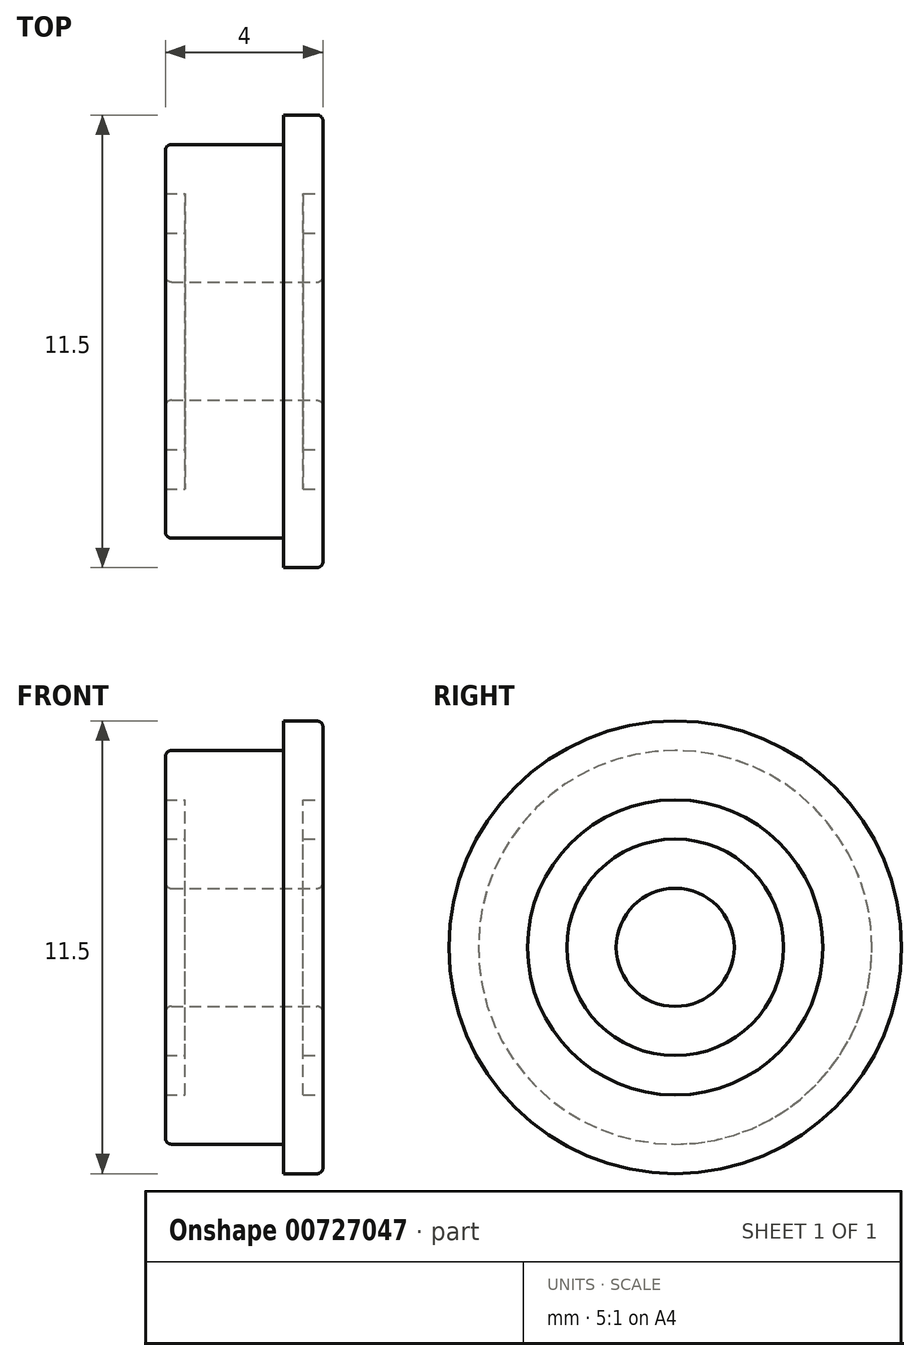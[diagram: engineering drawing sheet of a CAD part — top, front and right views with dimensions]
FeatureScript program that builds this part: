
annotation { "Feature Type Name" : "Feature", "Feature Type Description" : "" }
export const myFeature = defineFeature(function(context is Context, id is Id, definition is map)
    precondition{}
    {
        {
            var Q0;
            Q0=qCreatedBy(makeId("Front.planeOp"),FACE);
            var sketch = newSketch(context, id + "F0", { "sketchPlane" : qUnion([Q0])});
            skLineSegment(sketch, "E0", {"start": v(-2, 1.5) * mm, "end": v(2, 1.5) * mm});
            skLineSegment(sketch, "E1", {"start": v(2, 1.5) * mm, "end": v(2, 2.75) * mm});
            skLineSegment(sketch, "E2", {"start": v(2, 3.75) * mm, "end": v(2, 5.75) * mm});
            skLineSegment(sketch, "E3", {"start": v(2, 5.75) * mm, "end": v(1, 5.75) * mm});
            skLineSegment(sketch, "E4", {"start": v(1, 5.75) * mm, "end": v(1, 5) * mm});
            skLineSegment(sketch, "E5", {"start": v(1, 5) * mm, "end": v(-2, 5) * mm});
            skLineSegment(sketch, "E6", {"start": v(-2, 5) * mm, "end": v(-2, 3.75) * mm});
            skLineSegment(sketch, "E7", {"start": v(-2, 3.75) * mm, "end": v(-1.5, 3.75) * mm});
            skLineSegment(sketch, "E8", {"start": v(-1.5, 3.75) * mm, "end": v(-1.5, 2.75) * mm});
            skLineSegment(sketch, "E9", {"start": v(-1.5, 2.75) * mm, "end": v(-2, 2.75) * mm});
            skLineSegment(sketch, "E10", {"start": v(-2, 2.75) * mm, "end": v(-2, 1.5) * mm});
            skLineSegment(sketch, "E11", {"start": v(0, 0) * mm, "end": v(-5.84, 0) * mm, "construction": true});
            skLineSegment(sketch, "E12", {"start": v(2, 3.75) * mm, "end": v(1.5, 3.75) * mm});
            skLineSegment(sketch, "E13", {"start": v(1.5, 3.75) * mm, "end": v(1.5, 2.75) * mm});
            skLineSegment(sketch, "E14", {"start": v(1.5, 2.75) * mm, "end": v(2, 2.75) * mm});
            skSolve(sketch);
        }
        {
            var Q0;
            Q0=makeQuery(id+"F0.imprint","IMPRINT",FACE,{"disambiguationData":[TD([[makeQuery(id+"F0.imprint","IMPRINT",EDGE,{"derivedFrom":sQuery(id+"F0.wireOp",EDGE,"E0")}),1.0]])]});
            var Q1;
            Q1=sQuery(id+"F0.wireOp",EDGE,"E11");
            revolve(context, id + "F1", {"surfaceOperationType" : NewSurfaceOperationType.NEW, "entities" : qUnion([Q0]), "axis" : qUnion([Q1]), "revolveType" : RevolveType.FULL});
        }
        {
            var Q0;
            Q0=makeQuery(id+"F1.opRevolve","SWEPT_EDGE",EDGE,{"disambiguationData":[OSD([sQuery(id+"F0.wireOp",EDGE,"E5"),sQuery(id+"F0.wireOp",EDGE,"E6")])]});
            var Q1;
            Q1=makeQuery(id+"F1.opRevolve","SWEPT_EDGE",EDGE,{"disambiguationData":[OSD([sQuery(id+"F0.wireOp",EDGE,"E2"),sQuery(id+"F0.wireOp",EDGE,"E3")])]});
            var Q2;
            Q2=makeQuery(id+"F1.opRevolve","SWEPT_EDGE",EDGE,{"disambiguationData":[OSD([sQuery(id+"F0.wireOp",EDGE,"E0"),sQuery(id+"F0.wireOp",EDGE,"E10")])]});
            var Q3;
            Q3=makeQuery(id+"F1.opRevolve","SWEPT_EDGE",EDGE,{"disambiguationData":[OSD([sQuery(id+"F0.wireOp",EDGE,"E0"),sQuery(id+"F0.wireOp",EDGE,"E1")])]});
            fillet(context, id + "F2", {"entities" : qUnion([Q0, Q1, Q2, Q3]), "radius" : 0.15 * mm, "tangentPropagation" : true, "allowEdgeOverflow" : false});
        }
    });
